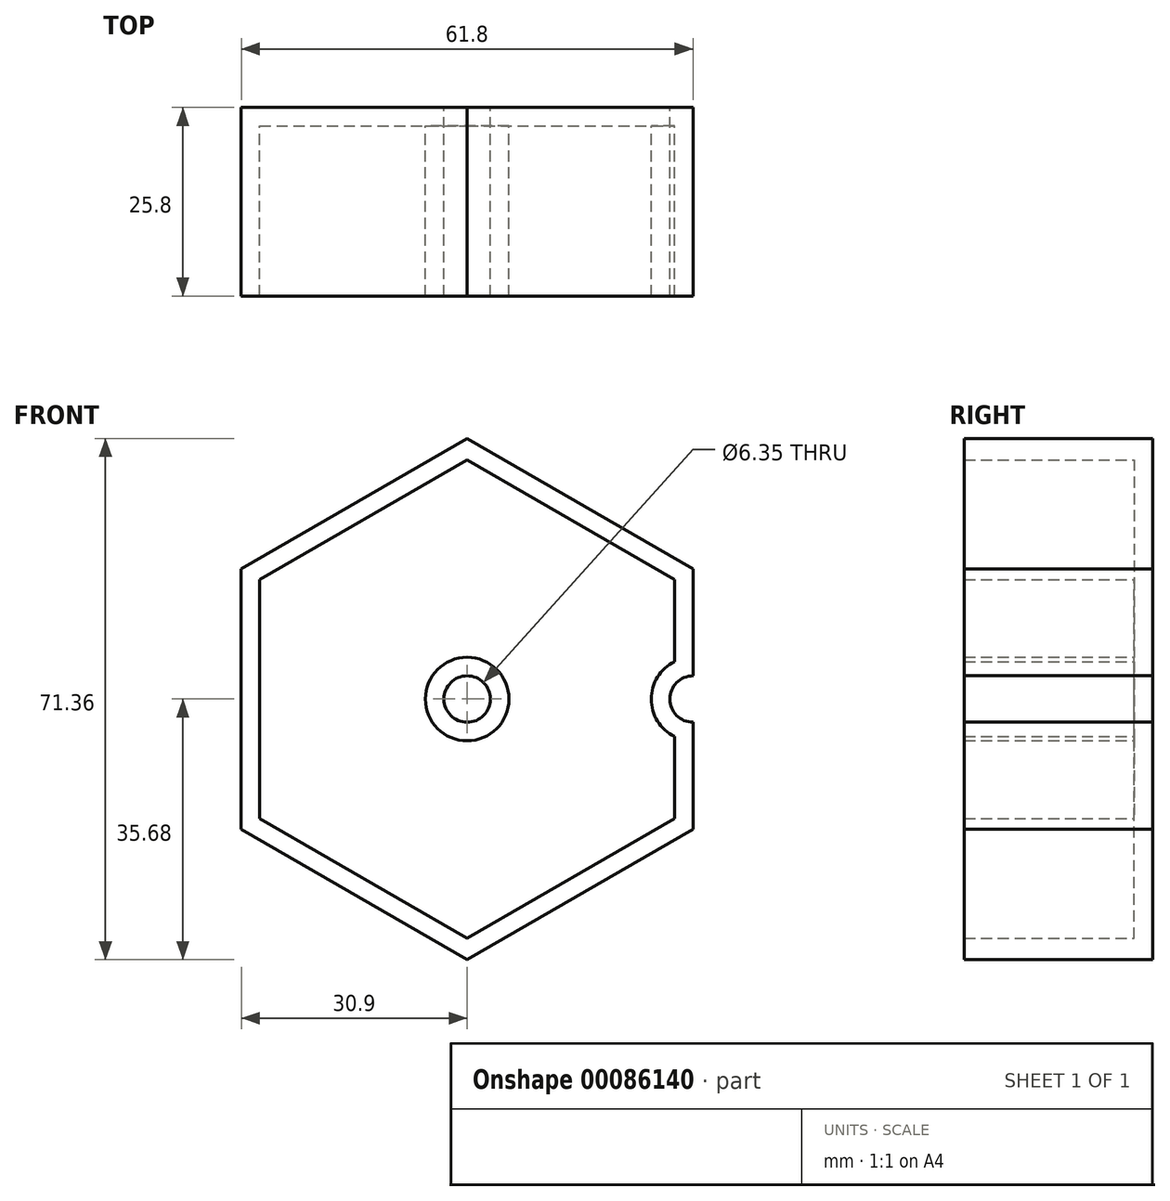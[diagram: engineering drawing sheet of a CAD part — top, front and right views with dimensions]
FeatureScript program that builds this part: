
annotation { "Feature Type Name" : "Feature", "Feature Type Description" : "" }
export const myFeature = defineFeature(function(context is Context, id is Id, definition is map)
    precondition{}
    {
        {
            var Q0;
            Q0=qCreatedBy(makeId("Front.planeOp"),FACE);
            var sketch = newSketch(context, id + "F0", { "sketchPlane" : qUnion([Q0])});
            skCircle(sketch, "E0", {"center": v(0, 0) * mm, "radius": 30.9 * mm});
            skCircle(sketch, "E1.cCircle", {"center": v(0, 0) * mm, "radius": 30.9 * mm, "construction": true});
            skLineSegment(sketch, "E1.0", {"start": v(30.9, 17.84) * mm, "end": v(30.9, -17.84) * mm});
            skLineSegment(sketch, "E1.1", {"start": v(30.9, -17.84) * mm, "end": v(0, -35.68) * mm});
            skLineSegment(sketch, "E1.2", {"start": v(0, -35.68) * mm, "end": v(-30.9, -17.84) * mm});
            skLineSegment(sketch, "E1.3", {"start": v(-30.9, -17.84) * mm, "end": v(-30.9, 17.84) * mm});
            skLineSegment(sketch, "E1.4", {"start": v(-30.9, 17.84) * mm, "end": v(0, 35.68) * mm});
            skLineSegment(sketch, "E1.5", {"start": v(0, 35.68) * mm, "end": v(30.9, 17.84) * mm});
            skPoint(sketch, "E1.0.midPoint", {"position": v(30.9, 0) * mm});
            skSolve(sketch);
        }
        {
            var Q0;
            {var subQ0=sQuery(id+"F0.wireOp",EDGE,"E1.5");var subQ1=sQuery(id+"F0.wireOp",EDGE,"E0");var subQ2=makeQuery(id+"F0.imprint","INTERSECT",VERTEX,{"derivedFrom":[subQ1,subQ0]});Q0=makeQuery(id+"F0.imprint","IMPRINT",FACE,{"disambiguationData":[TD([[makeQuery(id+"F0.imprint","IMPRINT",EDGE,{"disambiguationData":[TD([[subQ2,1.0]])],"derivedFrom":subQ1}),-1.0]])]});}
            var Q1;
            {var subQ0=sQuery(id+"F0.wireOp",EDGE,"E1.5");var subQ1=sQuery(id+"F0.wireOp",EDGE,"E0");var subQ2=makeQuery(id+"F0.imprint","INTERSECT",VERTEX,{"derivedFrom":[subQ1,subQ0]});Q1=makeQuery(id+"F0.imprint","IMPRINT",FACE,{"disambiguationData":[TD([[makeQuery(id+"F0.imprint","IMPRINT",EDGE,{"disambiguationData":[TD([[subQ2,-1.0]])],"derivedFrom":subQ1}),-1.0]])]});}
            var Q2;
            {var subQ0=sQuery(id+"F0.wireOp",EDGE,"E1.4");var subQ1=sQuery(id+"F0.wireOp",EDGE,"E0");var subQ2=makeQuery(id+"F0.imprint","INTERSECT",VERTEX,{"derivedFrom":[subQ1,subQ0]});Q2=makeQuery(id+"F0.imprint","IMPRINT",FACE,{"disambiguationData":[TD([[makeQuery(id+"F0.imprint","IMPRINT",EDGE,{"disambiguationData":[TD([[subQ2,-1.0]])],"derivedFrom":subQ1}),-1.0]])]});}
            var Q3;
            {var subQ0=sQuery(id+"F0.wireOp",EDGE,"E1.3");var subQ1=sQuery(id+"F0.wireOp",EDGE,"E0");var subQ2=makeQuery(id+"F0.imprint","INTERSECT",VERTEX,{"derivedFrom":[subQ1,subQ0]});Q3=makeQuery(id+"F0.imprint","IMPRINT",FACE,{"disambiguationData":[TD([[makeQuery(id+"F0.imprint","IMPRINT",EDGE,{"disambiguationData":[TD([[subQ2,-1.0]])],"derivedFrom":subQ1}),-1.0]])]});}
            var Q4;
            {var subQ0=sQuery(id+"F0.wireOp",EDGE,"E1.2");var subQ1=sQuery(id+"F0.wireOp",EDGE,"E0");var subQ2=makeQuery(id+"F0.imprint","INTERSECT",VERTEX,{"derivedFrom":[subQ1,subQ0]});Q4=makeQuery(id+"F0.imprint","IMPRINT",FACE,{"disambiguationData":[TD([[makeQuery(id+"F0.imprint","IMPRINT",EDGE,{"disambiguationData":[TD([[subQ2,-1.0]])],"derivedFrom":subQ1}),-1.0]])]});}
            var Q5;
            {var subQ0=sQuery(id+"F0.wireOp",EDGE,"E1.0");var subQ1=sQuery(id+"F0.wireOp",EDGE,"E0");var subQ2=makeQuery(id+"F0.imprint","INTERSECT",VERTEX,{"derivedFrom":[subQ1,subQ0]});Q5=makeQuery(id+"F0.imprint","IMPRINT",FACE,{"disambiguationData":[TD([[makeQuery(id+"F0.imprint","IMPRINT",EDGE,{"disambiguationData":[TD([[subQ2,1.0]])],"derivedFrom":subQ1}),-1.0]])]});}
            var Q6;
            {var subQ0=sQuery(id+"F0.wireOp",EDGE,"E0");var subQ4=makeQuery(id+"F0.imprint","INTERSECT",VERTEX,{"derivedFrom":[subQ0,sQuery(id+"F0.wireOp",EDGE,"E1.5")]});Q6=makeQuery(id+"F0.imprint","IMPRINT",FACE,{"disambiguationData":[TD([[makeQuery(id+"F0.imprint","IMPRINT",EDGE,{"disambiguationData":[TD([[subQ4,1.0]])],"derivedFrom":subQ0}),1.0]])]});}
            extrude(context, id + "F1", {"entities" : qUnion([Q0, Q1, Q2, Q3, Q4, Q5, Q6]), "depth" : 25.8 * mm});
        }
        {
            var Q0;
            {var subQ0=sQuery(id+"F0.wireOp",EDGE,"E0");var subQ4=makeQuery(id+"F0.imprint","INTERSECT",VERTEX,{"derivedFrom":[subQ0,sQuery(id+"F0.wireOp",EDGE,"E1.5")]});Q0=makeQuery(id+"F0.imprint","IMPRINT",FACE,{"disambiguationData":[TD([[makeQuery(id+"F0.imprint","IMPRINT",EDGE,{"disambiguationData":[TD([[subQ4,1.0]])],"derivedFrom":subQ0}),1.0]])]});}
            extrude(context, id + "F2", {"entities" : qUnion([Q0]), "operationType" : NewBodyOperationType.ADD, "depth" : 21.73 * mm});
        }
        {
            var Q0;
            Q0=sQuery(id+"F0.wireOp",VERTEX,"E0.center");
            var Q1;
            Q1=sQuery(id+"F0.wireOp",VERTEX,"E1.0.midPoint");
            var Q2;
            Q2=makeQuery(id+"F1.opExtrude","SWEPT_BODY",BODY,{"disambiguationData":[OSD([sQuery(id+"F0.wireOp",EDGE,"E1.0"),sQuery(id+"F0.wireOp",EDGE,"E1.1"),sQuery(id+"F0.wireOp",EDGE,"E1.2"),sQuery(id+"F0.wireOp",EDGE,"E1.3"),sQuery(id+"F0.wireOp",EDGE,"E1.4"),sQuery(id+"F0.wireOp",EDGE,"E1.5")])]});
            hole(context, id + "F3", {"style" : HoleStyle.SIMPLE, "endStyle" : HoleEndStyle.THROUGH, "oppositeDirection" : true, "holeDiameter" : 6.35 * mm, "locations" : qUnion([Q0, Q1]), "scope" : qUnion([Q2]), "isTappedThrough" : true});
        }
        {
            var Q0;
            Q0=makeQuery(id+"F1.opExtrude","CAP_FACE",FACE,{"disambiguationData":[OSD([sQuery(id+"F0.wireOp",EDGE,"E1.0"),sQuery(id+"F0.wireOp",EDGE,"E1.1"),sQuery(id+"F0.wireOp",EDGE,"E1.2"),sQuery(id+"F0.wireOp",EDGE,"E1.3"),sQuery(id+"F0.wireOp",EDGE,"E1.4"),sQuery(id+"F0.wireOp",EDGE,"E1.5")])],"isStart":false});
            shell(context, id + "F4", {"entities" : qUnion([Q0]), "thickness" : 2.54 * mm});
        }
    });
